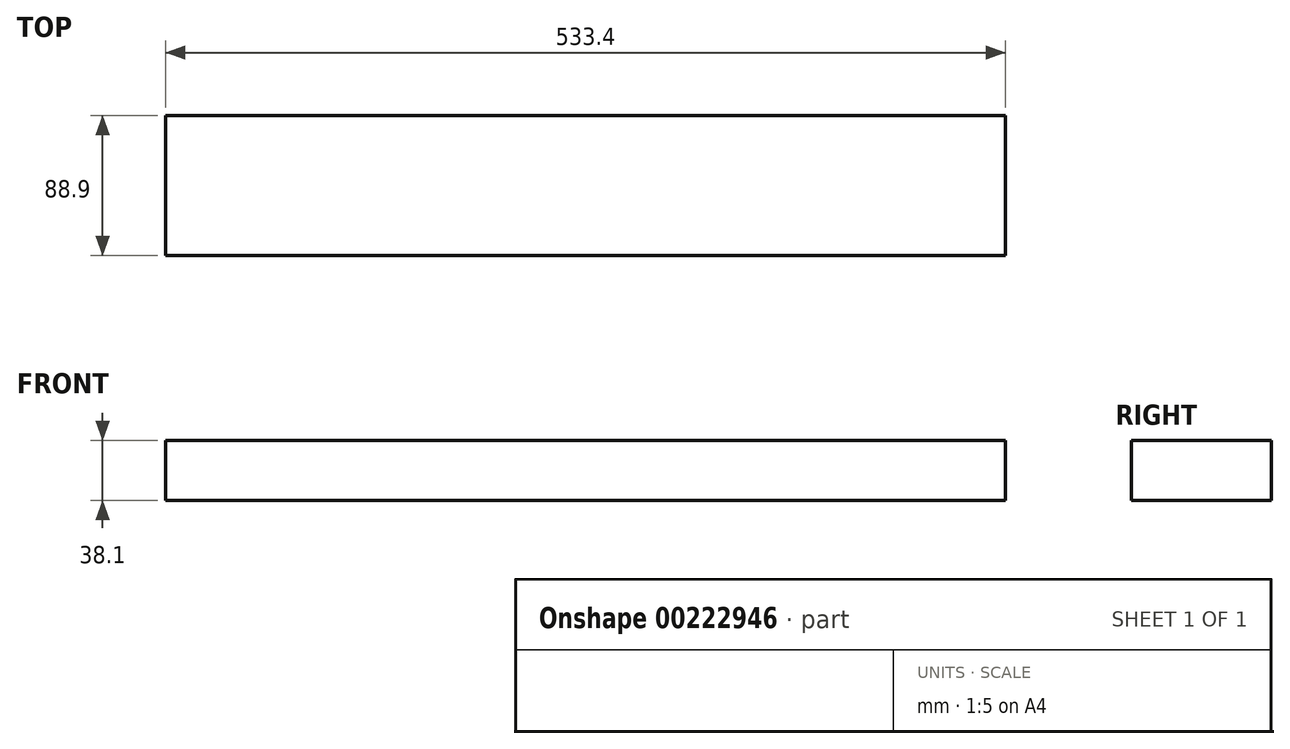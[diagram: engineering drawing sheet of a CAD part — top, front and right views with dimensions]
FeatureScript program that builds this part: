
annotation { "Feature Type Name" : "Feature", "Feature Type Description" : "" }
export const myFeature = defineFeature(function(context is Context, id is Id, definition is map)
    precondition{}
    {
        {
            var Q0;
            Q0=qCreatedBy(makeId("Top.planeOp"),FACE);
            var sketch = newSketch(context, id + "F0", { "sketchPlane" : qUnion([Q0])});
            skLineSegment(sketch, "E0.bottom", {"start": v(0, 0) * mm, "end": v(533.4, 0) * mm});
            skLineSegment(sketch, "E0.top", {"start": v(0, 88.9) * mm, "end": v(533.4, 88.9) * mm});
            skLineSegment(sketch, "E0.left", {"start": v(0, 0) * mm, "end": v(0, 88.9) * mm});
            skLineSegment(sketch, "E0.right", {"start": v(533.4, 0) * mm, "end": v(533.4, 88.9) * mm});
            skSolve(sketch);
        }
        {
            var Q0;
            Q0 = qSketchRegion(id + "F0", true);
            extrude(context, id + "F1", {"entities" : qUnion([Q0]), "depth" : 38.1 * mm});
        }
    });
